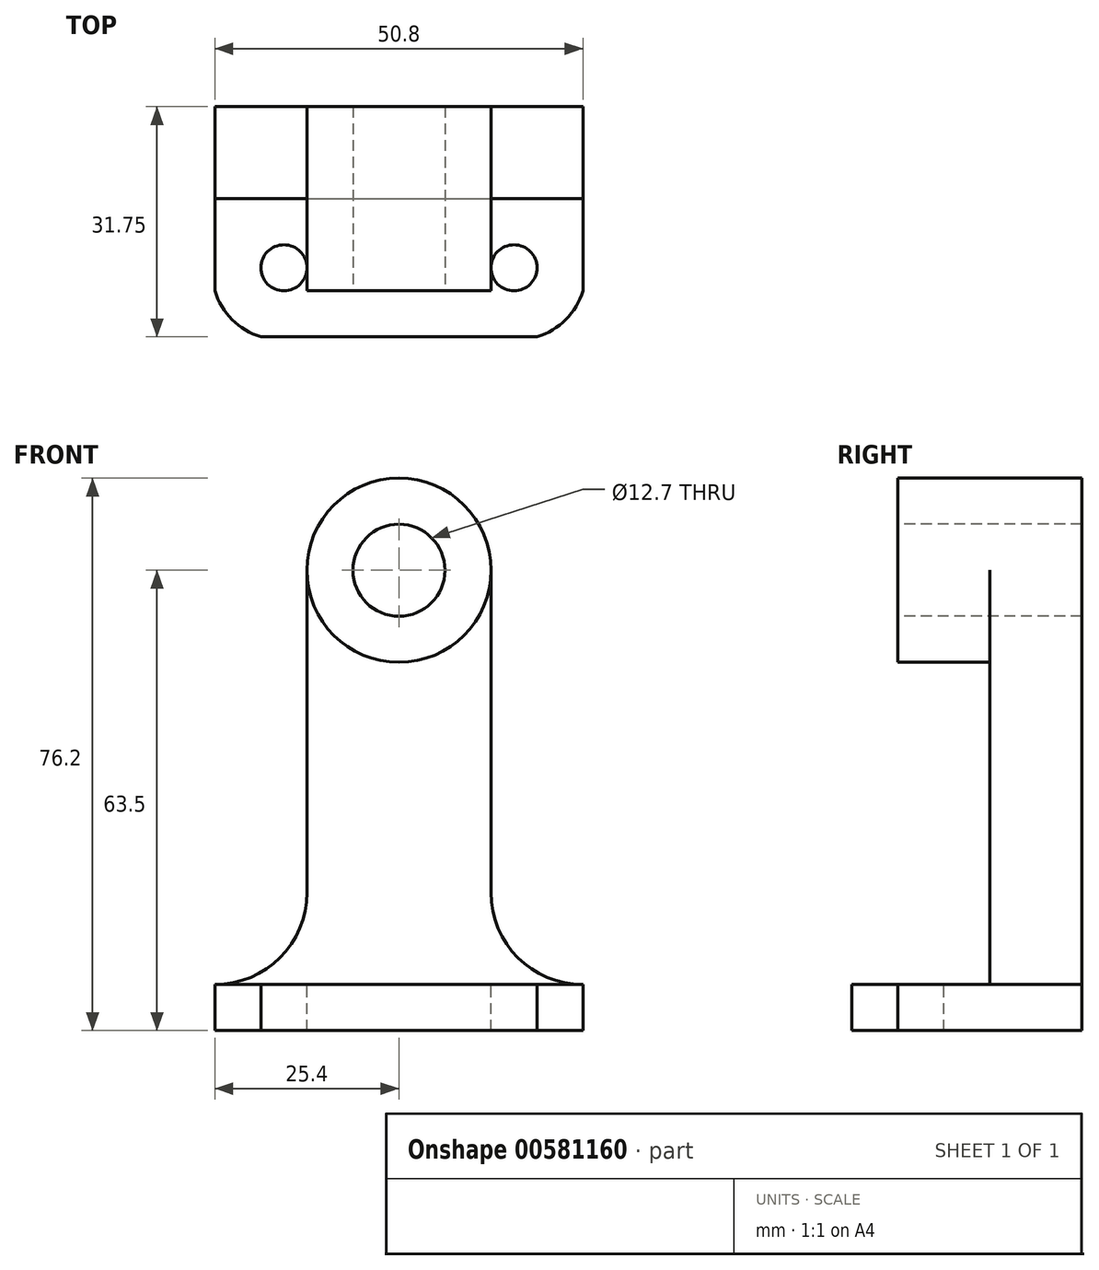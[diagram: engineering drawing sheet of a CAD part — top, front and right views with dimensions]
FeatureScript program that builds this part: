
annotation { "Feature Type Name" : "Feature", "Feature Type Description" : "" }
export const myFeature = defineFeature(function(context is Context, id is Id, definition is map)
    precondition{}
    {
        {
            var Q0;
            Q0=qCreatedBy(makeId("Front.planeOp"),FACE);
            var sketch = newSketch(context, id + "F0", { "sketchPlane" : qUnion([Q0])});
            skLineSegment(sketch, "E0", {"start": v(0, 0) * mm, "end": v(50.8, 0) * mm});
            skLineSegment(sketch, "E1", {"start": v(50.8, 0) * mm, "end": v(50.8, 19.05) * mm});
            skLineSegment(sketch, "E2", {"start": v(50.8, 19.05) * mm, "end": v(38.1, 19.05) * mm});
            skLineSegment(sketch, "E3", {"start": v(38.1, 19.05) * mm, "end": v(38.1, 76.2) * mm});
            skLineSegment(sketch, "E4", {"start": v(38.1, 76.2) * mm, "end": v(12.7, 76.2) * mm});
            skLineSegment(sketch, "E5", {"start": v(12.7, 76.2) * mm, "end": v(12.7, 19.05) * mm});
            skLineSegment(sketch, "E6", {"start": v(12.7, 19.05) * mm, "end": v(0, 19.05) * mm});
            skLineSegment(sketch, "E7", {"start": v(0, 19.05) * mm, "end": v(0, 0) * mm});
            skSolve(sketch);
        }
        {
            var Q0;
            Q0=makeQuery(id+"F0.imprint","IMPRINT",FACE,{"disambiguationData":[TD([[makeQuery(id+"F0.imprint","IMPRINT",EDGE,{"derivedFrom":sQuery(id+"F0.wireOp",EDGE,"E0")}),1.0]])]});
            extrude(context, id + "F1", {"entities" : qUnion([Q0]), "depth" : 12.7 * mm, "offsetDistance" : 25.4 * mm});
        }
        {
            var Q0;
            Q0=makeQuery(id+"F1.opExtrude","CAP_FACE",FACE,{"disambiguationData":[OSD([sQuery(id+"F0.wireOp",EDGE,"E0"),sQuery(id+"F0.wireOp",EDGE,"E1"),sQuery(id+"F0.wireOp",EDGE,"E2"),sQuery(id+"F0.wireOp",EDGE,"E3"),sQuery(id+"F0.wireOp",EDGE,"E4"),sQuery(id+"F0.wireOp",EDGE,"E5"),sQuery(id+"F0.wireOp",EDGE,"E6"),sQuery(id+"F0.wireOp",EDGE,"E7")])],"isStart":false});
            var sketch = newSketch(context, id + "F2", { "sketchPlane" : qUnion([Q0])});
            skLineSegment(sketch, "E8", {"start": v(0, 6.35) * mm, "end": v(50.8, 6.35) * mm});
            skSolve(sketch);
        }
        {
            var Q0;
            {var subQ0=sQuery(id+"F2.wireOp",EDGE,"E8");Q0=makeQuery(id+"F2.imprint","IMPRINT",FACE,{"disambiguationData":[TD([[makeQuery(id+"F2.imprint","IMPRINT",EDGE,{"derivedFrom":subQ0}),-1.0]])]});}
            extrude(context, id + "F3", {"entities" : qUnion([Q0]), "operationType" : NewBodyOperationType.ADD, "depth" : 19.05 * mm, "offsetDistance" : 25.4 * mm});
        }
        {
            var Q0;
            Q0=makeQuery(id+"F1.opExtrude","CAP_FACE",FACE,{"disambiguationData":[OSD([sQuery(id+"F0.wireOp",EDGE,"E0"),sQuery(id+"F0.wireOp",EDGE,"E1"),sQuery(id+"F0.wireOp",EDGE,"E2"),sQuery(id+"F0.wireOp",EDGE,"E3"),sQuery(id+"F0.wireOp",EDGE,"E4"),sQuery(id+"F0.wireOp",EDGE,"E5"),sQuery(id+"F0.wireOp",EDGE,"E6"),sQuery(id+"F0.wireOp",EDGE,"E7")])],"isStart":false});
            var sketch = newSketch(context, id + "F4", { "sketchPlane" : qUnion([Q0])});
            skArc(sketch, "E9", {"start": v(38.1, 19.05) * mm, "mid": v(41.82, 10.07) * mm, "end": v(50.8, 6.35) * mm});
            skArc(sketch, "E10", {"start": v(0, 6.35) * mm, "mid": v(8.98, 10.07) * mm, "end": v(12.7, 19.05) * mm});
            skSolve(sketch);
        }
        {
            var Q0;
            Q0=makeQuery(id+"F4.imprint","IMPRINT",FACE,{"disambiguationData":[TD([[makeQuery(id+"F4.imprint","IMPRINT",EDGE,{"derivedFrom":sQuery(id+"F4.wireOp",EDGE,"E10")}),1.0]])]});
            var Q1;
            Q1=makeQuery(id+"F4.imprint","IMPRINT",FACE,{"disambiguationData":[TD([[makeQuery(id+"F4.imprint","IMPRINT",EDGE,{"derivedFrom":sQuery(id+"F4.wireOp",EDGE,"E9")}),1.0]])]});
            extrude(context, id + "F5", {"entities" : qUnion([Q0, Q1]), "operationType" : NewBodyOperationType.REMOVE, "oppositeDirection" : true, "depth" : 12.7 * mm, "offsetDistance" : 25.4 * mm});
        }
        {
            var Q0;
            Q0=makeQuery(id+"F3.opExtrude","SWEPT_FACE",FACE,{"disambiguationData":[OSD([sQuery(id+"F2.wireOp",EDGE,"E8")])]});
            var sketch = newSketch(context, id + "F6", { "sketchPlane" : qUnion([Q0])});
            skArc(sketch, "E11", {"start": v(44.45, -31.75) * mm, "mid": v(48.42, -29.37) * mm, "end": v(50.8, -25.4) * mm});
            skArc(sketch, "E12", {"start": v(0, -25.4) * mm, "mid": v(2.38, -29.37) * mm, "end": v(6.35, -31.75) * mm});
            skSolve(sketch);
        }
        {
            var Q0;
            Q0=qCreatedBy(makeId("Front.planeOp"),FACE);
            var sketch = newSketch(context, id + "F7", { "sketchPlane" : qUnion([Q0])});
            skCircle(sketch, "E13", {"center": v(25.4, 63.5) * mm, "radius": 12.7 * mm});
            skSolve(sketch);
        }
        {
            var Q0;
            Q0=makeQuery(id+"F7.imprint","IMPRINT",FACE,{"disambiguationData":[TD([[makeQuery(id+"F7.imprint","IMPRINT",EDGE,{"derivedFrom":sQuery(id+"F7.wireOp",EDGE,"E13")}),1.0]])]});
            extrude(context, id + "F8", {"entities" : qUnion([Q0]), "operationType" : NewBodyOperationType.ADD, "depth" : 25.4 * mm, "offsetDistance" : 25.4 * mm});
        }
        {
            var Q0;
            Q0=makeQuery(id+"F8.opExtrude","CAP_FACE",FACE,{"disambiguationData":[OSD([sQuery(id+"F7.wireOp",EDGE,"E13")])],"isStart":false});
            var sketch = newSketch(context, id + "F9", { "sketchPlane" : qUnion([Q0])});
            skCircle(sketch, "E14", {"center": v(25.4, 63.5) * mm, "radius": 6.35 * mm});
            skSolve(sketch);
        }
        {
            var Q0;
            Q0=makeQuery(id+"F9.imprint","IMPRINT",FACE,{"disambiguationData":[TD([[makeQuery(id+"F9.imprint","IMPRINT",EDGE,{"derivedFrom":sQuery(id+"F9.wireOp",EDGE,"E14")}),1.0]])]});
            var Q1;
            {var subQ0=sQuery(id+"F0.wireOp",EDGE,"E4");var subQ1=sQuery(id+"F0.wireOp",EDGE,"E3");var subQ2=makeQuery(id+"F1.opExtrude","CAP_FACE",FACE,{"disambiguationData":[OSD([sQuery(id+"F0.wireOp",EDGE,"E0"),sQuery(id+"F0.wireOp",EDGE,"E1"),sQuery(id+"F0.wireOp",EDGE,"E2"),subQ1,subQ0,sQuery(id+"F0.wireOp",EDGE,"E5"),sQuery(id+"F0.wireOp",EDGE,"E6"),sQuery(id+"F0.wireOp",EDGE,"E7")])],"isStart":false});Q1=makeQuery(id+"F8.boolean.opBoolean","SPLIT",FACE,{"disambiguationData":[TD([subQ2,makeQuery(id+"F1.opExtrude","SWEPT_FACE",FACE,{"disambiguationData":[OSD([subQ1])]}),makeQuery(id+"F1.opExtrude","SWEPT_FACE",FACE,{"disambiguationData":[OSD([subQ0])]}),makeQuery(id+"F8.opExtrude","SWEPT_FACE",FACE,{"disambiguationData":[OSD([sQuery(id+"F7.wireOp",EDGE,"E13")])]})])],"derivedFrom":subQ2});}
            var Q2;
            {var subQ0=sQuery(id+"F0.wireOp",EDGE,"E5");var subQ1=sQuery(id+"F0.wireOp",EDGE,"E4");var subQ2=makeQuery(id+"F1.opExtrude","CAP_FACE",FACE,{"disambiguationData":[OSD([sQuery(id+"F0.wireOp",EDGE,"E0"),sQuery(id+"F0.wireOp",EDGE,"E1"),sQuery(id+"F0.wireOp",EDGE,"E2"),sQuery(id+"F0.wireOp",EDGE,"E3"),subQ1,subQ0,sQuery(id+"F0.wireOp",EDGE,"E6"),sQuery(id+"F0.wireOp",EDGE,"E7")])],"isStart":false});Q2=makeQuery(id+"F8.boolean.opBoolean","SPLIT",FACE,{"disambiguationData":[TD([subQ2,makeQuery(id+"F1.opExtrude","SWEPT_FACE",FACE,{"disambiguationData":[OSD([subQ1])]}),makeQuery(id+"F1.opExtrude","SWEPT_FACE",FACE,{"disambiguationData":[OSD([subQ0])]}),makeQuery(id+"F8.opExtrude","SWEPT_FACE",FACE,{"disambiguationData":[OSD([sQuery(id+"F7.wireOp",EDGE,"E13")])]})])],"derivedFrom":subQ2});}
            extrude(context, id + "F10", {"entities" : qUnion([Q0, Q1, Q2]), "operationType" : NewBodyOperationType.REMOVE, "oppositeDirection" : true, "depth" : 25.4 * mm, "offsetDistance" : 25.4 * mm});
        }
        {
            var Q0;
            Q0=makeQuery(id+"F3.opExtrude","SWEPT_FACE",FACE,{"disambiguationData":[OSD([sQuery(id+"F2.wireOp",EDGE,"E8")])]});
            var sketch = newSketch(context, id + "F11", { "sketchPlane" : qUnion([Q0])});
            skCircle(sketch, "E15", {"center": v(41.28, -22.23) * mm, "radius": 3.17 * mm});
            skCircle(sketch, "E16", {"center": v(9.53, -22.23) * mm, "radius": 3.18 * mm});
            skSolve(sketch);
        }
        {
            var Q0;
            {var subQ0=sQuery(id+"F6.wireOp",EDGE,"E12");Q0=makeQuery(id+"F6.imprint","IMPRINT",FACE,{"disambiguationData":[TD([[makeQuery(id+"F6.imprint","IMPRINT",EDGE,{"derivedFrom":subQ0}),-1.0]])]});}
            var Q1;
            {var subQ0=sQuery(id+"F6.wireOp",EDGE,"E11");Q1=makeQuery(id+"F6.imprint","IMPRINT",FACE,{"disambiguationData":[TD([[makeQuery(id+"F6.imprint","IMPRINT",EDGE,{"derivedFrom":subQ0}),-1.0]])]});}
            var Q2;
            Q2=makeQuery(id+"F11.imprint","IMPRINT",FACE,{"disambiguationData":[TD([[makeQuery(id+"F11.imprint","IMPRINT",EDGE,{"derivedFrom":sQuery(id+"F11.wireOp",EDGE,"E16")}),1.0]])]});
            var Q3;
            Q3=makeQuery(id+"F11.imprint","IMPRINT",FACE,{"disambiguationData":[TD([[makeQuery(id+"F11.imprint","IMPRINT",EDGE,{"derivedFrom":sQuery(id+"F11.wireOp",EDGE,"E15")}),1.0]])]});
            extrude(context, id + "F12", {"entities" : qUnion([Q0, Q1, Q2, Q3]), "operationType" : NewBodyOperationType.REMOVE, "oppositeDirection" : true, "depth" : 6.35 * mm, "offsetDistance" : 25.4 * mm});
        }
    });
